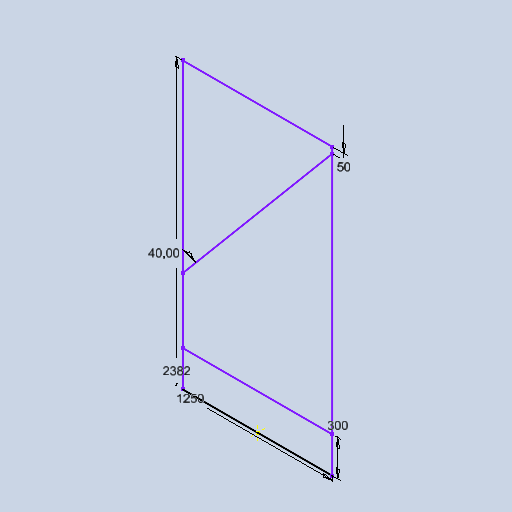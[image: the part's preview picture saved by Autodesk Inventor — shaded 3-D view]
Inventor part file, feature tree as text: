
AUTODESK INVENTOR PART (.ipt)
format: ipt  version: 2025 (Build 290162010, 162A)  size: 259,584 bytes
history: native  units: in
note: dims shown in document units (in); Inventor stores cm internally (conversion verified against a paired STEP export)
features: sketch x2
ambient origin geometry x8: Origin, YZ Plane, XZ Plane, XY Plane, X Axis, Y Axis, Z Axis, Center Point
feature tree (2):
  sketch  "Sketch3"  dims[d5=49.2126in d6=93.7795in d10=11.811in d11=1.9685in d12=0.2749in]
  sketch  "3D Sketch3"
